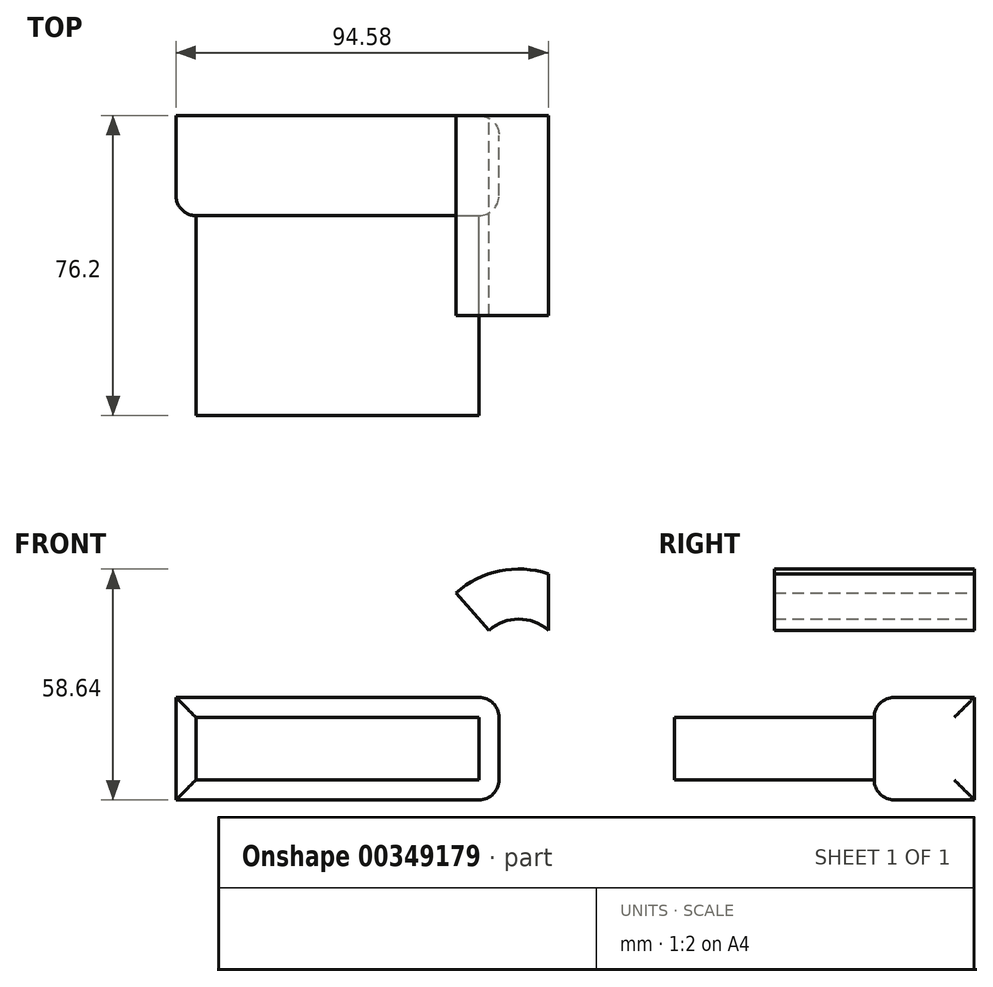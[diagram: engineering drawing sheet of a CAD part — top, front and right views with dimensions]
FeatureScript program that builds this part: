
annotation { "Feature Type Name" : "Feature", "Feature Type Description" : "" }
export const myFeature = defineFeature(function(context is Context, id is Id, definition is map)
    precondition{}
    {
        {
            var Q0;
            Q0=qCreatedBy(makeId("Front.planeOp"),FACE);
            var sketch = newSketch(context, id + "F0", { "sketchPlane" : qUnion([Q0])});
            skLineSegment(sketch, "E0.bottom", {"start": v(-61.03, 7.66) * mm, "end": v(18.51, 7.66) * mm});
            skLineSegment(sketch, "E0.top", {"start": v(-61.03, -18.37) * mm, "end": v(18.51, -18.37) * mm});
            skLineSegment(sketch, "E0.left", {"start": v(-61.03, 7.66) * mm, "end": v(-61.03, -18.37) * mm});
            skLineSegment(sketch, "E0.right", {"start": v(18.51, 7.66) * mm, "end": v(18.51, -18.37) * mm});
            skLineSegment(sketch, "E1.bottom", {"start": v(33.55, 60.3) * mm, "end": v(68.84, 60.3) * mm});
            skLineSegment(sketch, "E1.top", {"start": v(33.55, 24.73) * mm, "end": v(68.84, 24.73) * mm});
            skLineSegment(sketch, "E1.left", {"start": v(33.55, 60.3) * mm, "end": v(33.55, 24.73) * mm});
            skLineSegment(sketch, "E1.right", {"start": v(68.84, 60.3) * mm, "end": v(68.84, 24.73) * mm});
            skArc(sketch, "E2", {"start": v(18.51, 7.66) * mm, "mid": v(37.4, 16.2) * mm, "end": v(18.51, 24.73) * mm});
            skArc(sketch, "E3.0", {"start": v(10.11, -1.86) * mm, "mid": v(50.1, 16.2) * mm, "end": v(10.11, 34.26) * mm});
            skLineSegment(sketch, "E4", {"start": v(10.11, 34.26) * mm, "end": v(18.51, 24.73) * mm});
            skLineSegment(sketch, "E5", {"start": v(18.51, 7.66) * mm, "end": v(10.11, -1.86) * mm});
            skSolve(sketch);
        }
        {
            var Q0;
            Q0=makeQuery(id+"F0.imprint","IMPRINT",FACE,{"disambiguationData":[TD([[makeQuery(id+"F0.imprint","IMPRINT",EDGE,{"derivedFrom":sQuery(id+"F0.wireOp",EDGE,"E0.bottom")}),-1.0]])]});
            var Q1;
            {var subQ0=sQuery(id+"F0.wireOp",EDGE,"E5");Q1=makeQuery(id+"F0.imprint","IMPRINT",FACE,{"disambiguationData":[TD([[makeQuery(id+"F0.imprint","IMPRINT",EDGE,{"derivedFrom":subQ0}),1.0]])]});}
            extrude(context, id + "F1", {"entities" : qUnion([Q0, Q1]), "depth" : 25.4 * mm});
        }
        {
            var Q0;
            Q0=makeQuery(id+"F1.opExtrude","SWEPT_FACE",FACE,{"disambiguationData":[OSD([sQuery(id+"F0.wireOp",EDGE,"E0.right")])]});
            extrude(context, id + "F2", {"entities" : qUnion([Q0]), "operationType" : NewBodyOperationType.ADD, "depth" : 2.54 * mm});
        }
        {
            var Q0;
            Q0=makeQuery(id+"F2.opExtrude","CAP_FACE",FACE,{"disambiguationData":[OSD([sQuery(id+"F0.wireOp",EDGE,"E0.right")])],"isStart":false});
            var Q1;
            {var subQ0=sQuery(id+"F0.wireOp",EDGE,"E0.right");Q1=makeQuery(id+"F2.boolean.opBoolean","MERGE",FACE,{"derivedFrom":[makeQuery(id+"F1.opExtrude","CAP_FACE",FACE,{"disambiguationData":[OSD([sQuery(id+"F0.wireOp",EDGE,"E0.bottom"),sQuery(id+"F0.wireOp",EDGE,"E0.top"),sQuery(id+"F0.wireOp",EDGE,"E0.left"),subQ0])],"isStart":false}),makeQuery(id+"F2.opExtrude","SWEPT_FACE",FACE,{"disambiguationData":[OSD([subQ0]),TDD([makeQuery(id+"F1.opExtrude","CAP_EDGE",EDGE,{"disambiguationData":[OSD([subQ0])],"isStart":false})])]})]});}
            fillet(context, id + "F3", {"entities" : qUnion([Q0, Q1]), "radius" : 5.08 * mm, "tangentPropagation" : true, "allowEdgeOverflow" : false});
        }
        {
            var Q0;
            {var subQ5=sQuery(id+"F0.wireOp",EDGE,"E4");Q0=makeQuery(id+"F0.imprint","IMPRINT",FACE,{"disambiguationData":[TD([[makeQuery(id+"F0.imprint","IMPRINT",EDGE,{"derivedFrom":subQ5}),1.0]])]});}
            var Q1;
            {var subQ0=sQuery(id+"F0.wireOp",EDGE,"E0.right");Q1=makeQuery(id+"F2.boolean.opBoolean","MERGE",FACE,{"derivedFrom":[makeQuery(id+"F1.opExtrude","CAP_FACE",FACE,{"disambiguationData":[OSD([sQuery(id+"F0.wireOp",EDGE,"E0.bottom"),sQuery(id+"F0.wireOp",EDGE,"E0.top"),sQuery(id+"F0.wireOp",EDGE,"E0.left"),subQ0])],"isStart":false}),makeQuery(id+"F2.opExtrude","SWEPT_FACE",FACE,{"disambiguationData":[OSD([subQ0]),TDD([makeQuery(id+"F1.opExtrude","CAP_EDGE",EDGE,{"disambiguationData":[OSD([subQ0])],"isStart":false})])]})]});}
            extrude(context, id + "F4", {"entities" : qUnion([Q0, Q1]), "operationType" : NewBodyOperationType.ADD, "depth" : 50.8 * mm});
        }
    });
